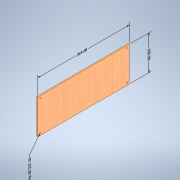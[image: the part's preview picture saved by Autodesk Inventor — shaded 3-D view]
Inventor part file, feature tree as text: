
AUTODESK INVENTOR PART (.ipt)
format: ipt  version: 2022 (Build 260153000, 153)  size: 137,728 bytes
history: native  units: mm
features: other x4, extrude x2, sketch x2, hole x1
ambient origin geometry x8: Origin, YZ Plane, XZ Plane, XY Plane, X Axis, Y Axis, Z Axis, Center Point
bodies: Solid1 (feature_tree)
feature tree (9):
  other  "Horizontal_Plate"
  other  "Annotations"
  extrude  "Front_Base"  Depth=100.0mm
  extrude  "Joint_Holes"  Depth=100.0mm
  sketch  "Sketch1"  dims[d0=264.68mm d1=100.0mm]
  sketch  "Sketch2"  dims[d2=3.175mm d3=0.0mm d4=3.3mm d5=6.6mm d6=6.6mm d7=6.6mm d8=6.6mm d9=0.0mm d10=0.0mm d11=5.203611mm d12=3.356478mm d13=264.68mm d14=9.218915mm d15=1.439094mm d16=100.0mm d17=20.548853mm]
  other  "Linear Dimension 1"
  other  "Linear Dimension 2"
  hole  "Hole Note 1"  [1 undecoded]
note: 1 required parameter value undecoded (feature->parameter linkage not recoverable at this tier; creation-order binding heuristic only, values carry confidence <= 0.55)
